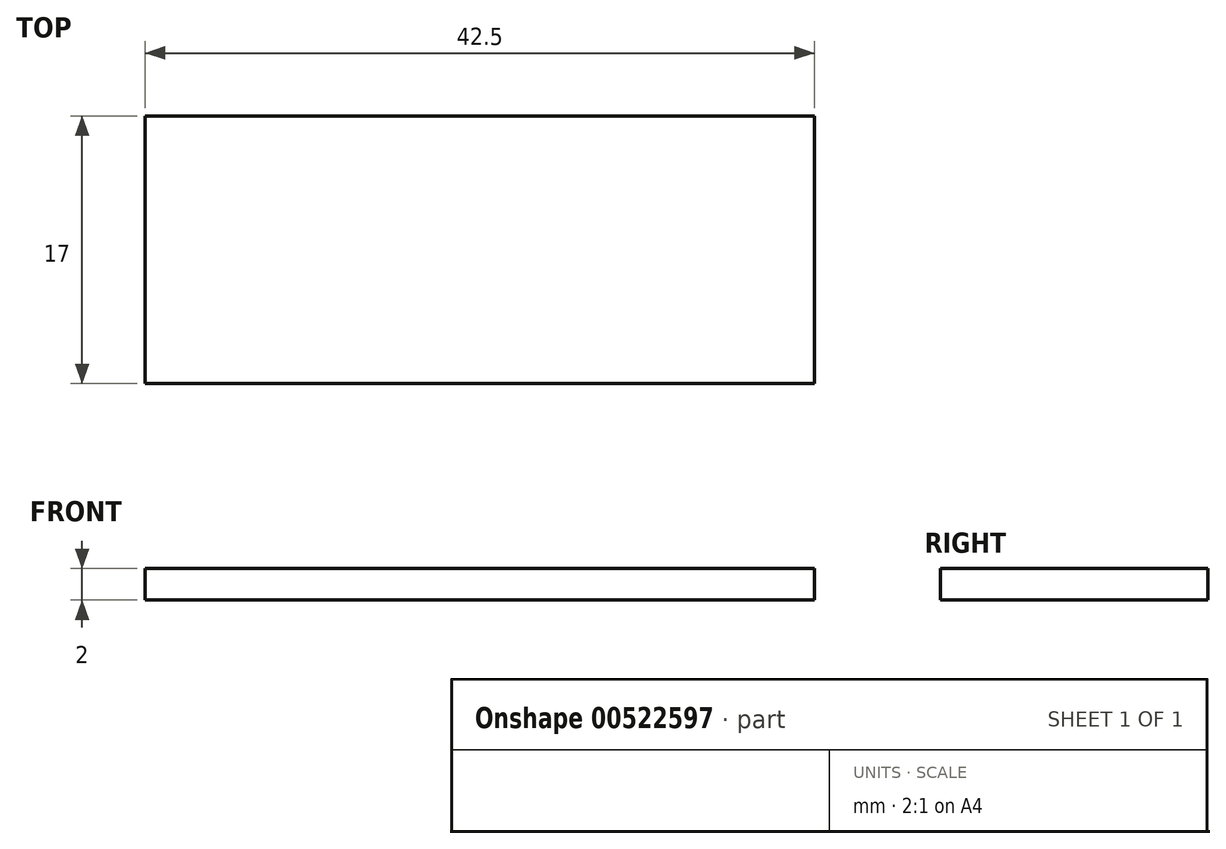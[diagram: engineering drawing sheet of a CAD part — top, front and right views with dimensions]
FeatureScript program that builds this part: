
annotation { "Feature Type Name" : "Feature", "Feature Type Description" : "" }
export const myFeature = defineFeature(function(context is Context, id is Id, definition is map)
    precondition{}
    {
        {
            var Q0;
            Q0=qCreatedBy(makeId("Top.planeOp"),FACE);
            var sketch = newSketch(context, id + "F0", { "sketchPlane" : qUnion([Q0])});
            skLineSegment(sketch, "E0.bottom", {"start": v(-21.25, 8.5) * mm, "end": v(21.25, 8.5) * mm});
            skLineSegment(sketch, "E0.top", {"start": v(-21.25, -8.5) * mm, "end": v(21.25, -8.5) * mm});
            skLineSegment(sketch, "E0.left", {"start": v(-21.25, 8.5) * mm, "end": v(-21.25, -8.5) * mm});
            skLineSegment(sketch, "E0.right", {"start": v(21.25, 8.5) * mm, "end": v(21.25, -8.5) * mm});
            skPoint(sketch, "E0.middle", {"position": v(0, 0) * mm});
            skSolve(sketch);
        }
        {
            var Q0;
            Q0 = qSketchRegion(id + "F0", true);
            extrude(context, id + "F1", {"entities" : qUnion([Q0]), "depth" : 2 * mm, "offsetDistance" : 25 * mm});
        }
    });
